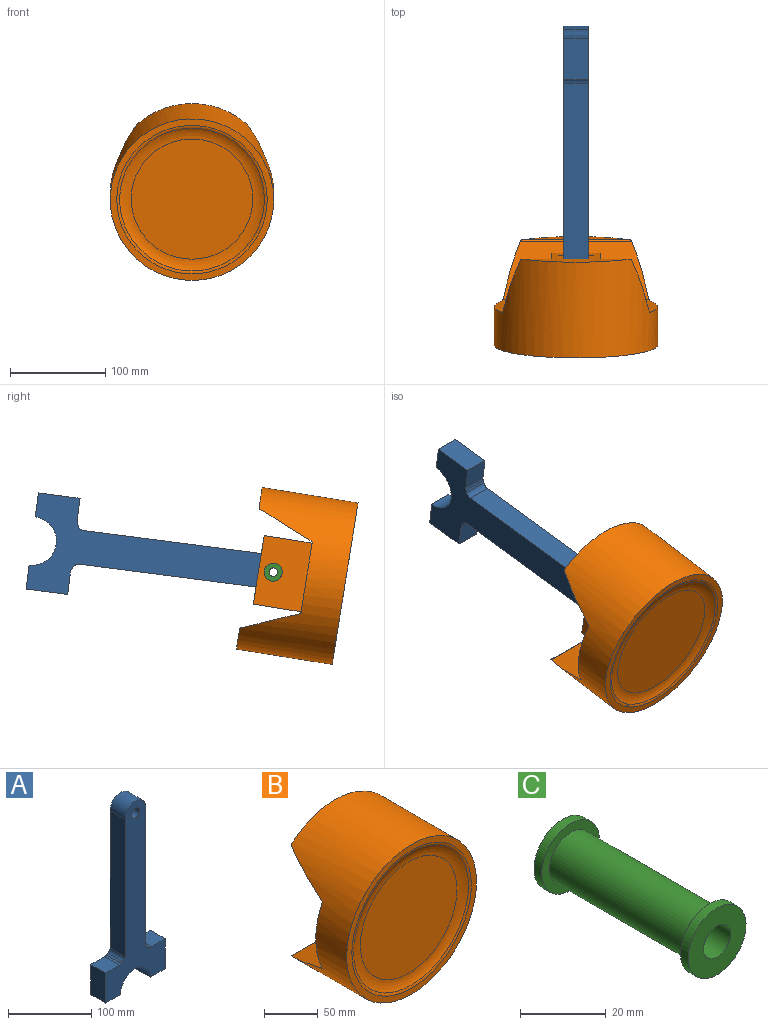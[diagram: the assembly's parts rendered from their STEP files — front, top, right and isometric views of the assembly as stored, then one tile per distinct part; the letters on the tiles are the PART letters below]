
ASSEMBLY  parts=3 mates=2
PART A: 19 faces, bbox 101.6x25.4x272.6 mm
  f0: cylinder r=6.35mm len=25.4mm, axis (0,1,0), area 79.5mm2, adj f1,f15,f17,f18
  f1: cylinder r=50.8mm len=25.4mm, axis (0,1,0), area 73.7mm2, adj f0,f2,f17,f18
  f2: cylinder r=6.35mm len=25.4mm, axis (0,1,0), area 183mm2, adj f1,f3,f17,f18
  f3: plane 203.03x25.4mm, normal (1,0,0), area 5157mm2, adj f2,f4,f17,f18
  f4: cylinder r=17.78mm len=35.56mm, axis (0,1,0), area 1418.8mm2, adj f3,f5,f17,f18
  f5: plane 203.03x25.4mm, normal (-1,0,0), area 5157mm2, adj f4,f6,f17,f18
  f6: cylinder r=6.35mm len=25.4mm, axis (0,1,0), area 183mm2, adj f5,f7,f17,f18
  f7: cylinder r=50.8mm len=25.4mm, axis (0,1,0), area 73.7mm2, adj f6,f8,f17,f18
  f8: cylinder r=6.35mm len=25.4mm, axis (0,1,0), area 79.5mm2, adj f7,f9,f17,f18
  f9: plane 25.4x23.75mm, normal (0,0,1), area 603.3mm2, adj f8,f10,f17,f18
  f10: plane 43.99x25.4mm, normal (-1,0,0), area 1117.4mm2, adj f9,f11,f17,f18
  f11: plane 25.4x25.4mm, normal (0,0,-1), area 645.2mm2, adj f10,f12,f17,f18
  f12: cylinder r=25.4mm len=50.8mm, axis (0,1,0), area 2026.8mm2, adj f11,f13,f17,f18
  f13: plane 25.4x25.4mm, normal (0,0,-1), area 645.2mm2, adj f12,f14,f17,f18
  f14: plane 43.99x25.4mm, normal (1,0,0), area 1117.4mm2, adj f13,f15,f17,f18
  f15: plane 25.4x23.75mm, normal (0,0,1), area 603.3mm2, adj f0,f14,f17,f18
  f16: cylinder r=6.99mm len=25.4mm, axis (0,1,0), area 1114.8mm2, adj f17,f18
  f17: plane 272.62x101.6mm, normal (0,-1,0), area 11333.1mm2, adj f0,f1,f2,f3,f4,f5,f6,f7
  f18: plane 272.62x101.6mm, normal (0,1,0), area 11333.1mm2, adj f0,f1,f2,f3,f4,f5,f6,f7
PART B: 31 faces, bbox 177.1x105.2x177.1 mm
  f0: cylinder r=6.99mm len=13.97mm, axis (-1,0,0), area 167.2mm2, adj f24,f26
  f1: cylinder r=9.53mm len=19.05mm, axis (-1,0,0), area 152mm2, adj f16,f24
  f2: plane 72.82x60.33mm, normal (0,1,0), area 4199.6mm2, adj f4,f10,f13,f18
  f3: plane 111.33x20.53mm, normal (0,1,0), area 1564.8mm2, adj f4,f14
  f4: cylinder r=85.72mm len=171.45mm, axis (0,1,0), area 41415mm2, adj f2,f3,f5,f6,f9,f10,f11,f12
  f5: plane 171.45x171.45mm, normal (0,-1,0), area 3557.1mm2, adj f4,f8
  f6: plane 111.33x20.53mm, normal (0,1,0), area 1564.8mm2, adj f4,f15
  f7: plane 127.53x127.53mm, normal (0,-1,0), area 12773.4mm2, adj f30
  f8: torus R=78.84mm, axis (0,-1,0), area 1526.5mm2, adj f5,f30
  f9: plane 72.82x60.33mm, normal (0,1,0), area 4199.6mm2, adj f4,f10,f13,f16
  f10: cylinder r=2.54mm len=155.22mm, axis (1,0,0), area 459.4mm2, adj f2,f4,f9,f11,f19
  f11: plane 152.93x57.66mm, normal (0,0.39,0.92), area 8561.7mm2, adj f4,f10,f14
  f12: plane 152.93x57.66mm, normal (0,0.39,-0.92), area 8561.7mm2, adj f4,f13,f15
  f13: cylinder r=2.54mm len=155.22mm, axis (1,0,0), area 459.4mm2, adj f2,f4,f9,f12,f17
  f14: cylinder r=2.54mm len=116.6mm, axis (1,0,0), area 341.3mm2, adj f3,f4,f11
  f15: cylinder r=2.54mm len=116.6mm, axis (1,0,0), area 341.3mm2, adj f4,f6,f12
  f16: plane 72.82x50.8mm, normal (-1,0,0), area 3414.1mm2, adj f1,f9,f17,f19,f20
  f17: plane 50.8x50.8mm, normal (0,0,1), area 2580.6mm2, adj f13,f16,f18,f20
  f18: plane 72.82x50.8mm, normal (1,0,0), area 3414.1mm2, adj f2,f17,f19,f20,f21
  f19: plane 50.8x50.8mm, normal (0,0,-1), area 2580.6mm2, adj f10,f16,f18,f20
  f20: plane 72.82x50.8mm, normal (0,1,0), area 1763.6mm2, adj f16,f17,f18,f19,f25,f26,f27,f28
  f21: cylinder r=9.53mm len=19.05mm, axis (-1,0,0), area 152mm2, adj f18,f23
  f22: cylinder r=6.99mm len=13.97mm, axis (-1,0,0), area 167.2mm2, adj f23,f28
  f23: plane 19.05x19.05mm, normal (1,0,0), area 131.7mm2, adj f21,f22
  f24: plane 19.05x19.05mm, normal (-1,0,0), area 131.7mm2, adj f0,f1
  f25: plane 40.82x38.1mm, normal (0,0,-1), area 1555.2mm2, adj f20,f26,f28,f29
  f26: plane 50.8x40.82mm, normal (1,0,0), area 1920.3mm2, adj f0,f20,f25,f27,f29
  f27: plane 40.82x38.1mm, normal (0,0,1), area 1555.2mm2, adj f20,f26,f28,f29
  f28: plane 50.8x40.82mm, normal (-1,0,0), area 1920.3mm2, adj f20,f22,f25,f27,f29
  f29: plane 50.8x38.1mm, normal (0,1,0), area 1935.5mm2, adj f25,f26,f27,f28
  f30: torus R=63.76mm, axis (0,1,0), area 5523.1mm2, adj f7,f8
PART C: 8 faces, bbox 19.1x50.8x19.1 mm
  f0: cylinder r=9.53mm len=19.05mm, axis (0,1,0), area 152mm2, adj f1,f3
  f1: plane 19.05x19.05mm, normal (0,1,0), area 223mm2, adj f0,f7
  f2: cylinder r=6.99mm len=45.72mm, axis (0,-1,0), area 2006.6mm2, adj f3,f4
  f3: plane 19.05x19.05mm, normal (0,-1,0), area 131.7mm2, adj f0,f2
  f4: plane 19.05x19.05mm, normal (0,1,0), area 131.7mm2, adj f2,f6
  f5: plane 19.05x19.05mm, normal (0,-1,0), area 223mm2, adj f6,f7
  f6: cylinder r=9.53mm len=19.05mm, axis (0,1,0), area 152mm2, adj f4,f5
  f7: cylinder r=4.45mm len=50.8mm, axis (0,-1,0), area 1418.8mm2, adj f1,f5
PLACE A rot(axis=(0.6,-0.6,0.53),124.3deg) t=(-20.9,224.09,-86.76)mm
PLACE B rot(axis=(1,0,0),9.1deg) t=(-8.2,-3.57,-115.41)mm
PLACE C rot(axis=(0.58,-0.58,0.58),120deg) t=(-8.2,-28.65,-119.43)mm
MATE revolute C.f0 <-> B.f1  axis (-1,0,0) through (17.2,-28.65,-119.43)mm
MATE revolute C.f2 <-> A.f4  axis (1,0,0) through (-8.2,-28.65,-119.43)mm
